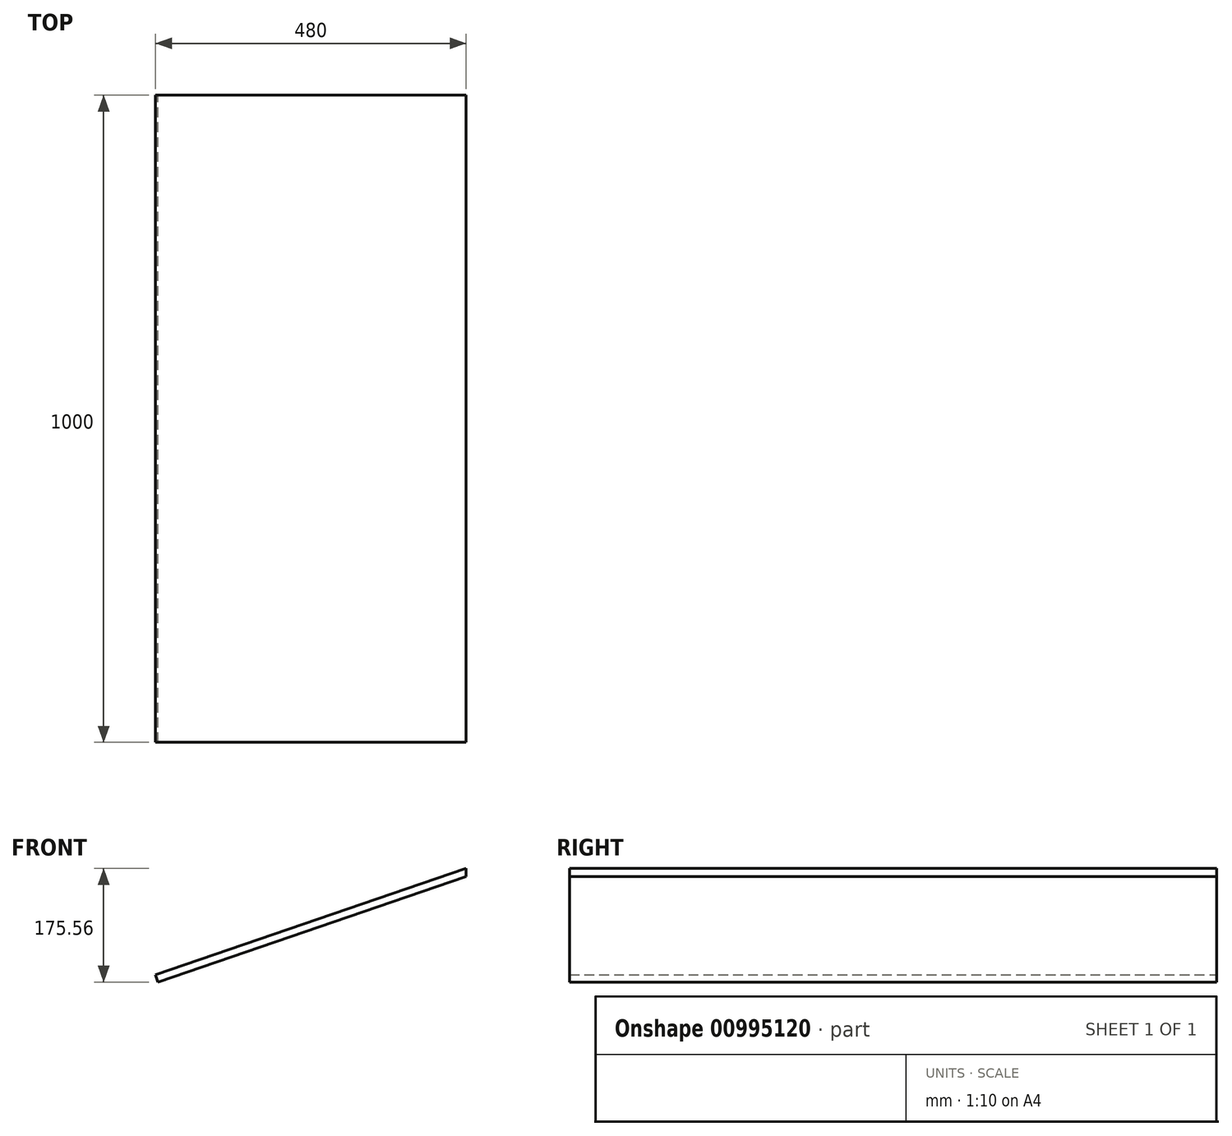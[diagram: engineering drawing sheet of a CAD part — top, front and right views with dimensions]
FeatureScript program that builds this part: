
annotation { "Feature Type Name" : "Feature", "Feature Type Description" : "" }
export const myFeature = defineFeature(function(context is Context, id is Id, definition is map)
    precondition{}
    {
        {
            var Q0;
            Q0=qCreatedBy(makeId("Front.planeOp"),FACE);
            var sketch = newSketch(context, id + "F0", { "sketchPlane" : qUnion([Q0])});
            skLineSegment(sketch, "E0", {"start": v(-380, 0) * mm, "end": v(-380, 350) * mm, "construction": true});
            skLineSegment(sketch, "E1", {"start": v(-476.12, 317.12) * mm, "end": v(0, 480) * mm});
            skLineSegment(sketch, "E2", {"start": v(0, 480) * mm, "end": v(380, 350) * mm, "construction": true});
            skLineSegment(sketch, "E3", {"start": v(380, 350) * mm, "end": v(380, 0) * mm, "construction": true});
            skLineSegment(sketch, "E4", {"start": v(380, 0) * mm, "end": v(-380, 0) * mm, "construction": true});
            skLineSegment(sketch, "E5.0", {"start": v(-480, 328.47) * mm, "end": v(0, 492.68) * mm});
            skLineSegment(sketch, "E6", {"start": v(0, 480) * mm, "end": v(0, 492.68) * mm});
            skLineSegment(sketch, "E7", {"start": v(-480, 328.47) * mm, "end": v(-476.12, 317.12) * mm});
            skSolve(sketch);
        }
        {
            var Q0;
            Q0=qSketchRegion(id+"F0",true);
            extrude(context, id + "F1", {"entities" : qUnion([Q0]), "depth" : 12 * mm, "offsetDistance" : 25 * mm});
        }
        {
            var Q0;
            Q0 = qSketchRegion(id + "F0", true);
            extrude(context, id + "F2", {"entities" : qUnion([Q0]), "operationType" : NewBodyOperationType.ADD, "depth" : 100 * mm, "offsetDistance" : 25 * mm, "hasSecondDirection" : true, "secondDirectionOppositeDirection" : true, "secondDirectionDepth" : 900 * mm});
        }
    });
